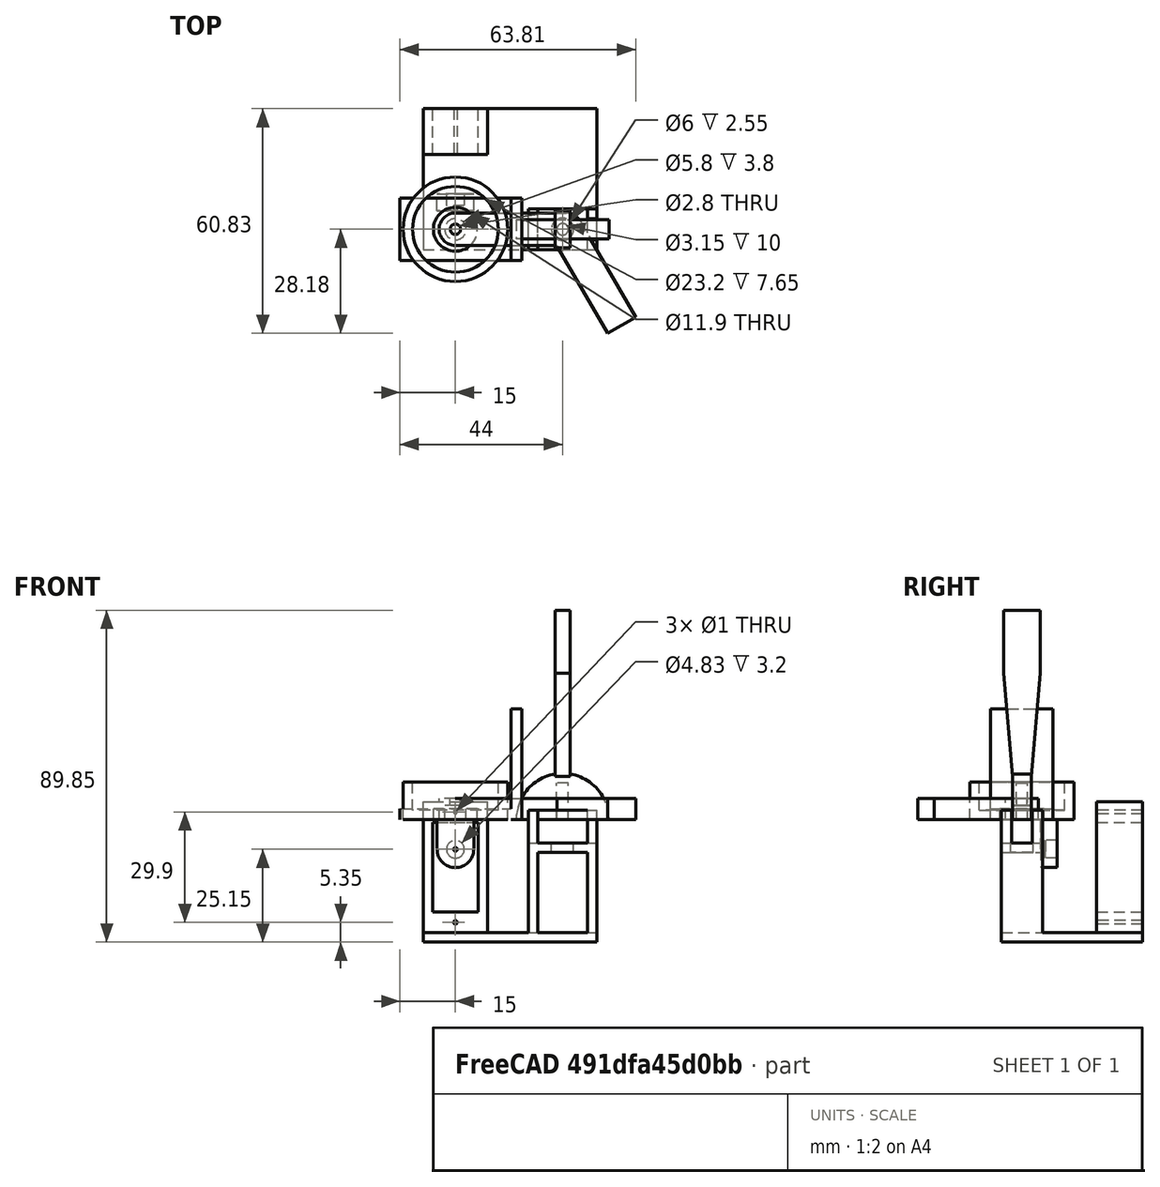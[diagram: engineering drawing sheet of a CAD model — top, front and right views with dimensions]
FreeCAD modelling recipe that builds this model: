
FCSTD DOCUMENT  (FreeCAD 0.18R16146 (Git))
Label: AnilloDedo
License: All rights reserved
LicenseURL: http://en.wikipedia.org/wiki/All_rights_reserved
objects: Part::Box×19, Part::Cylinder×15, Part::Cut×13, Part::MultiFuse×7, Spreadsheet::Sheet×1
note: 54 computed .brp shape members not serialized (recipe doc carries the construction recipe); baked Part::Feature solids carry a one-line shape summary decoded from their .brp

FEATURE [Spreadsheet::Sheet] Spreadsheet  label="v"
  cells = A1=Grosor; B1(Grosor)==2.55mm; A2=DiametroDedo; B2(DiametroDedo)==23.2mm; A3=AnilloMotorDiametro; B3(AnilloMotorDiametro)==4.83mm; A4=SeparacionDedoMotorGiro; B4(SeparacionDedoMotorGiro)==8mm; A5=AnilloMotorAlto; B5(AnilloMotorAlto)==3.2mm; A6=SeparacionDedoMotorHorizontal; B6(SeparacionDedoMotorHorizontal)==4.6mm; A7=PalancaSwitchDiametro; B7(PalancaSwitchDiametro)==3.15mm; A8=PalancaSwitchLargo; B8(PalancaSwitchLargo)==10mm; A9=SwitchDiametroRosca; B9(SwitchDiametroRosca)==6mm; A10=PalancaLargo; B10(PalancaLargo)==55mm; A11=PalancaAncho; B11(PalancaAncho)==10mm; A12=ServoAlto; B12(ServoAlto)==12.4mm; A13=ServoLargo; B13(ServoLargo)==22.4mm; A14=ServoAncho; B14(ServoAncho)==24.3mm; A15=ServoSeparacionTornillos; B15(ServoSeparacionTornillos)==26.8mm; A16=ServoAltoOreja; B16(ServoAltoOreja)==5.6mm; A17=ServoDistanciaEjeMotor; B17(ServoDistanciaEjeMotor)==17mm; A18=ServoDistanciaEjeOreja; B18(ServoDistanciaEjeOreja)==8.300000000000001mm; A19=ServoGrosorOreja; B19(ServoGrosorOreja)==2.4mm; A20=DistanciaDedoSwitch; B20(DistanciaDedoSwitch)==29mm; A21=SwitchLongRosca; B21(SwitchLongRosca)==8.800000000000001mm; A22=SwitchLargo; B22(SwitchLargo)==13.5mm
FEATURE [Part::Cylinder] Cylinder  label="PalancaHueco"
  Angle = 360
  AttacherType = Attacher::AttachEngine3D
  Height = 10
  Radius = 1.575
  expr: Height = v.PalancaSwitchLargo
  expr: Radius = v.PalancaSwitchDiametro / 2
FEATURE [Part::Cylinder] Cylinder001  label="PalancaCarril"
  Angle = 180
  AttacherType = Attacher::AttachEngine3D
  Height = 5.1
  Placement = pos=(0,2.55,0) rot=(1,0,0;1.5708rad)
  Radius = 12.55
  expr: Placement.Base.y = PalancaCarril.Height / 2
  expr: Radius = PalancaHueco.Height + v.Grosor
  expr: Height = v.Grosor * 2
FEATURE [Part::Box] Box  label="PalancaPala"
  AttacherType = Attacher::AttachEngine3D
  Height = 45
  Length = 4.125
  Placement = pos=(-2.0625,-5,11.7) rot=(0,0,1;0rad)
  Width = 10
  expr: Placement.Base.z = PalancaCarril.Radius - v.Grosor / 3
  expr: Placement.Base.y = -PalancaPala.Width / 2
  expr: Length = v.Grosor + v.PalancaSwitchDiametro / 2
  expr: Width = v.PalancaAncho
  expr: Placement.Base.x = -PalancaPala.Length / 2
  expr: Height = v.PalancaLargo - v.PalancaSwitchLargo
FEATURE [Part::Box] Box001  label="PalancaPalaQuita"
  AttacherType = Attacher::AttachEngine3D
  Height = 45
  Length = 4.125
  Placement = pos=(-2.0625,2.55,11.7) rot=(-1,0,0;0.087266rad)
  Width = 10
  expr: Placement.Base.z = PalancaPala.Placement.Base.z
  expr: Placement.Base.y = PalancaCarril.Height / 2
  expr: Placement.Base.x = PalancaPala.Placement.Base.x
  expr: Height = PalancaPala.Height
  expr: Width = PalancaPala.Width
  expr: Length = PalancaPala.Length
FEATURE [Part::Box] Box002  label="PalancaPalaQuita001"
  AttacherType = Attacher::AttachEngine3D
  Height = 45
  Length = 4.125
  Placement = pos=(2.0625,-2.55,11.7) rot=(0,-0.043619,0.999048;3.14159rad)
  Width = 10
  expr: Placement.Base.z = PalancaPala.Placement.Base.z
  expr: Placement.Base.y = -PalancaCarril.Height / 2
  expr: Placement.Base.x = PalancaPalaQuita001.Length / 2
  expr: Height = PalancaPala.Height
  expr: Width = PalancaPala.Width
  expr: Length = PalancaPala.Length
FEATURE [Part::Cut] Cut
  Base = -> Box
  Tool = -> Box001
FEATURE [Part::Cut] Cut001
  Base = -> Cut
  Tool = -> Box002
FEATURE [Part::MultiFuse] Fusion
  Shapes = -> [Cut001,Cylinder001]
FEATURE [Part::Cut] Cut002  label="Palanca"
  Base = -> Fusion
  Placement = pos=(29,0,0) rot=(0,0,1;0rad)
  Refine = true
  Tool = -> Cylinder
  expr: Placement.Base.x = TaladroSwitch.Placement.Base.x
FEATURE [Part::Cylinder] Cylinder002  label="AnilloInterior"
  Angle = 360
  AttacherType = Attacher::AttachEngine3D
  Height = 7.65
  Placement = pos=(0,0,2.55) rot=(0,0,1;0rad)
  Radius = 11.6
  expr: Placement.Base.z = v.Grosor
  expr: Height = v.Grosor * 3
  expr: Radius = v.DiametroDedo / 2
FEATURE [Part::Cylinder] Cylinder003  label="AnilloExterior"
  Angle = 360
  AttacherType = Attacher::AttachEngine3D
  Height = 10.2
  Radius = 14.15
  expr: Height = AnilloInterior.Height + v.Grosor
  expr: Radius = AnilloInterior.Radius + v.Grosor
FEATURE [Part::Cylinder] Cylinder004  label="MotorInterior"
  Angle = 360
  AttacherType = Attacher::AttachEngine3D
  Height = 3.2
  Placement = pos=(0,9.55,-8) rot=(1,0,0;1.5708rad)
  Radius = 2.415
  expr: Placement.Base.z = -v.SeparacionDedoMotorGiro
  expr: Placement.Base.y = AnilloExterior.Radius - v.SeparacionDedoMotorHorizontal
  expr: Height = v.AnilloMotorAlto
  expr: Radius = v.AnilloMotorDiametro / 2
FEATURE [Part::Cylinder] Cylinder005  label="MotorExterior"
  Angle = 360
  AttacherType = Attacher::AttachEngine3D
  Height = 4.475
  Placement = pos=(0,9.55,-8) rot=(1,0,0;1.5708rad)
  Radius = 4.965
  expr: Placement.Base.z = MotorInterior.Placement.Base.z
  expr: Placement.Base.y = MotorInterior.Placement.Base.y
  expr: Placement.Base.x = MotorInterior.Placement.Base.x
  expr: Height = MotorInterior.Height + v.Grosor / 2
  expr: Radius = MotorInterior.Radius + v.Grosor
FEATURE [Part::Cylinder] Cylinder006  label="TaladroTornilloAnilloMotor"
  Angle = 360
  AttacherType = Attacher::AttachEngine3D
  Height = 8.95
  Placement = pos=(0,9.55,-8) rot=(1,0,0;1.5708rad)
  Radius = 0.5
  expr: Placement.Base.z = MotorInterior.Placement.Base.z
  expr: Placement.Base.y = MotorInterior.Placement.Base.y
  expr: Placement.Base.x = MotorInterior.Placement.Base.x
  expr: Height = MotorExterior.Height * 2
  expr: Radius = 0.5mm
FEATURE [Part::Box] Box003  label="Radio"
  AttacherType = Attacher::AttachEngine3D
  Height = 8
  Length = 9.93
  Placement = pos=(-4.965,5.075,-8) rot=(0,0,1;0rad)
  Width = 4.475
  expr: Length = MotorExterior.Radius * 2
  expr: Width = MotorExterior.Height
  expr: Placement.Base.z = MotorInterior.Placement.Base.z
  expr: Placement.Base.y = MotorInterior.Placement.Base.y - Radio.Width
  expr: Height = MotorExterior.Placement.Base.z * -1
  expr: Placement.Base.x = MotorInterior.Placement.Base.x - Radio.Length / 2
FEATURE [Part::MultiFuse] Fusion001
  Shapes = -> [Cylinder003,Box003,Cylinder005]
FEATURE [Part::Cut] Cut003
  Base = -> Fusion001
  Tool = -> Cylinder002
FEATURE [Part::Cut] Cut004
  Base = -> Cut003
  Tool = -> Cylinder004
FEATURE [Part::Cut] Cut005  label="SoporteDedo"
  Base = -> Cut004
  Tool = -> Cylinder006
FEATURE [Part::Box] Box004  label="BaseServo"
  AttacherType = Attacher::AttachEngine3D
  Height = 5.6
  Length = 12.4
  Placement = pos=(-6.2,20.25,-30.6) rot=(0,0,1;0rad)
  Width = 12.4
  expr: Placement.Base.y = MotorInterior.Placement.Base.y + v.ServoDistanciaEjeOreja + v.ServoGrosorOreja
  expr: Placement.Base.z = TaladroTornilloAnilloMotor.Placement.Base.z - BaseServo.Height - v.ServoDistanciaEjeMotor
  expr: Length = v.ServoAlto
  expr: Width = v.ServoAlto
  expr: Placement.Base.x = -BaseServo.Length / 2
  expr: Height = v.ServoAltoOreja
FEATURE [Part::Cylinder] Cylinder007  label="TaladroAnclajeServo"
  Angle = 360
  AttacherType = Attacher::AttachEngine3D
  Height = 12.4
  Placement = pos=(0,32.65,-27.8) rot=(1,0,0;1.5708rad)
  Radius = 0.5
  expr: Placement.Base.y = BaseServo.Placement.Base.y + BaseServo.Width
  expr: Placement.Base.z = BaseServo.Placement.Base.z + BaseServo.Height / 2
  expr: Height = BaseServo.Width
  expr: Radius = TaladroTornilloAnilloMotor.Radius
FEATURE [Part::Box] Box005  label="LadoCajaServo"
  AttacherType = Attacher::AttachEngine3D
  Height = 35.5
  Length = 2.55
  Placement = pos=(-8.75,20.25,-30.6) rot=(0,0,1;0rad)
  Width = 12.4
  expr: Placement.Base.z = BaseServo.Placement.Base.z
  expr: Placement.Base.y = BaseServo.Placement.Base.y
  expr: Placement.Base.x = BaseServo.Placement.Base.x - v.Grosor
  expr: Height = BaseServo.Height + v.ServoAncho + TopServo.Height
  expr: Length = v.Grosor
  expr: Width = BaseServo.Width
FEATURE [Part::Box] Box006  label="LadoCajaServo001"
  AttacherType = Attacher::AttachEngine3D
  Height = 35.5
  Length = 2.55
  Placement = pos=(6.2,20.25,-30.6) rot=(0,0,1;0rad)
  Width = 12.4
  expr: Placement.Base.z = BaseServo.Placement.Base.z
  expr: Placement.Base.y = BaseServo.Placement.Base.y
  expr: Placement.Base.x = BaseServo.Placement.Base.x - v.Grosor + BaseServo.Width + v.Grosor
  expr: Height = BaseServo.Height + v.ServoAncho + TopServo.Height
  expr: Length = v.Grosor
  expr: Width = BaseServo.Width
FEATURE [Part::Box] Box007  label="TopServo"
  AttacherType = Attacher::AttachEngine3D
  Height = 5.6
  Length = 12.4
  Placement = pos=(-6.2,20.25,-0.7) rot=(0,0,1;0rad)
  Width = 12.4
  expr: Placement.Base.z = BaseServo.Placement.Base.z + v.ServoAncho + TopServo.Height
  expr: Placement.Base.y = BaseServo.Placement.Base.y
  expr: Placement.Base.x = BaseServo.Placement.Base.x
  expr: Height = BaseServo.Height
  expr: Width = BaseServo.Width
  expr: Length = BaseServo.Length
FEATURE [Part::Cylinder] Cylinder008  label="TaladroAnclajeServo001"
  Angle = 360
  AttacherType = Attacher::AttachEngine3D
  Height = 12.4
  Placement = pos=(0,32.65,2.1) rot=(1,0,0;1.5708rad)
  Radius = 0.5
  expr: Placement.Base.y = TopServo.Placement.Base.y + TopServo.Width
  expr: Placement.Base.z = TopServo.Placement.Base.z + TopServo.Height / 2
  expr: Height = BaseServo.Width
  expr: Radius = TaladroTornilloAnilloMotor.Radius
FEATURE [Part::Cylinder] Cylinder009  label="TaladroSwitch"
  Angle = 360
  AttacherType = Attacher::AttachEngine3D
  Height = 7.65
  Placement = pos=(29,0,-8.8) rot=(0,0,1;0rad)
  Radius = 3
  expr: Placement.Base.z = -v.SwitchLongRosca
  expr: Placement.Base.x = v.DistanciaDedoSwitch
  expr: Height = v.Grosor * 3
  expr: Radius = v.SwitchDiametroRosca / 2
FEATURE [Part::Box] Box008  label="BaseSwitch"
  AttacherType = Attacher::AttachEngine3D
  Height = 2.55
  Length = 13.5
  Placement = pos=(22.25,-5.55,-8.8) rot=(0,0,1;0rad)
  Width = 11.1
  expr: Placement.Base.z = TaladroSwitch.Placement.Base.z
  expr: Placement.Base.y = TaladroSwitch.Placement.Base.y - BaseSwitch.Width / 2
  expr: Length = v.SwitchLargo
  expr: Width = v.SwitchDiametroRosca + v.Grosor * 2
  expr: Placement.Base.x = TaladroSwitch.Placement.Base.x - BaseSwitch.Length / 2
  expr: Height = v.Grosor
FEATURE [Part::Box] Box009  label="Suelo"
  AttacherType = Attacher::AttachEngine3D
  Height = 2.55
  Length = 47.05
  Placement = pos=(-8.75,32.65,-30.6) rot=(1,0,0;3.14159rad)
  Width = 38.2
  expr: Length = -Suelo.Placement.Base.x + BaseSwitch001.Placement.Base.x + BaseSwitch001.Length + v.Grosor
  expr: Width = Suelo.Placement.Base.y + BaseSwitch001.Width / 2
  expr: Placement.Base.z = LadoCajaServo.Placement.Base.z
  expr: Placement.Base.y = LadoCajaServo.Placement.Base.y + LadoCajaServo.Width
  expr: Placement.Base.x = LadoCajaServo.Placement.Base.x
  expr: Height = v.Grosor
FEATURE [Part::Box] Box010  label="LadoCajaSwitch"
  AttacherType = Attacher::AttachEngine3D
  Height = 33.15
  Length = 2.55
  Placement = pos=(19.7,-5.55,-30.6) rot=(0,0,1;0rad)
  Width = 11.1
  expr: Placement.Base.y = BaseSwitch001.Placement.Base.y
  expr: Placement.Base.z = Suelo.Placement.Base.z
  expr: Placement.Base.x = BaseSwitch001.Placement.Base.x - v.Grosor
  expr: Height = -Suelo.Placement.Base.z + v.Grosor
  expr: Length = v.Grosor
  expr: Width = BaseSwitch001.Width
FEATURE [Part::Box] Box011  label="LadoCajaSwitch001"
  AttacherType = Attacher::AttachEngine3D
  Height = 33.15
  Length = 2.55
  Placement = pos=(35.75,-5.55,-30.6) rot=(0,0,1;0rad)
  Width = 11.1
  expr: Placement.Base.y = BaseSwitch001.Placement.Base.y
  expr: Placement.Base.z = Suelo.Placement.Base.z
  expr: Placement.Base.x = BaseSwitch001.Placement.Base.x + BaseSwitch001.Length
  expr: Height = -Suelo.Placement.Base.z + v.Grosor
  expr: Length = v.Grosor
  expr: Width = BaseSwitch001.Width
FEATURE [Part::Box] Box012  label="BaseSwitch001"
  AttacherType = Attacher::AttachEngine3D
  Height = 2.55
  Length = 13.5
  Placement = pos=(22.25,-5.55,0) rot=(0,0,1;0rad)
  Width = 11.1
  expr: Width = BaseSwitch.Width
  expr: Length = BaseSwitch.Length
  expr: Placement.Base.z = BaseSwitch.Placement.Base.z + v.SwitchLongRosca
  expr: Placement.Base.y = BaseSwitch.Placement.Base.y
  expr: Placement.Base.x = BaseSwitch.Placement.Base.x
  expr: Height = v.Grosor
FEATURE [Part::Box] Box013  label="QuitaCarril"
  AttacherType = Attacher::AttachEngine3D
  Height = 11.35
  Length = 18.6
  Placement = pos=(19.7,-2.8,-6.25) rot=(0,0,1;0rad)
  Width = 5.6
  expr: Placement.Base.z = BaseSwitch.Placement.Base.z + v.Grosor
  expr: Placement.Base.y = BaseSwitch.Placement.Base.y + (BaseSwitch.Width - QuitaCarril.Width) / 2
  expr: Length = BaseSwitch.Length + v.Grosor * 2
  expr: Width = PalancaCarril.Height + 0.5mm
  expr: Placement.Base.x = BaseSwitch.Placement.Base.x - v.Grosor
  expr: Height = v.Grosor + v.SwitchLongRosca
FEATURE [Part::MultiFuse] Fusion002  label="BaseSinTaladar"
  Shapes = -> [Box011,Box010,Box008,Box009,Box007,Box006,Box005,Box004]
FEATURE [Part::Cut] Cut006
  Base = -> Fusion002
  Tool = -> Box013
FEATURE [Part::Cut] Cut007
  Base = -> Cut006
  Tool = -> Cylinder009
FEATURE [Part::Cut] Cut008
  Base = -> Cut007
  Tool = -> Cylinder008
FEATURE [Part::Cut] Cut009  label="SoporteConjunto"
  Base = -> Cut008
  Tool = -> Cylinder007
FEATURE [Part::Cylinder] Cylinder010  label="InteriorServoGrande"
  Angle = 360
  AttacherType = Attacher::AttachEngine3D
  Height = 3.8
  Radius = 2.9
  expr: Radius = (5.9 - 0.1) / 2
FEATURE [Part::Cylinder] Cylinder011  label="ExteriorServoGrande"
  Angle = 360
  AttacherType = Attacher::AttachEngine3D
  Height = 5.8
  Radius = 4.4
  expr: Height = InteriorServoGrande.Height + 2mm
  expr: Radius = InteriorServoGrande.Radius + 1.5mm
FEATURE [Part::Cylinder] Cylinder012  label="TaladroServoGrande"
  Angle = 360
  AttacherType = Attacher::AttachEngine3D
  Height = 5.8
  Radius = 1.4
  expr: Height = ExteriorServoGrande.Height
  expr: Radius = 2.8 / 2
FEATURE [Part::Box] Box014  label="BaseRadioServoGrande"
  AttacherType = Attacher::AttachEngine3D
  Height = 5.8
  Length = 30
  Placement = pos=(0,-4.4,0) rot=(0,0,1;0rad)
  Width = 8.8
  expr: Placement.Base.y = -BaseRadioServoGrande.Width / 2
  expr: Width = ExteriorServoGrande.Radius * 2
  expr: Placement.Base.x = 0
  expr: Height = ExteriorServoGrande.Height
FEATURE [Part::MultiFuse] Fusion003
  Shapes = -> [Box014,Cylinder011]
FEATURE [Part::Cut] Cut010
  Base = -> Fusion003
  Tool = -> Cylinder012
FEATURE [Part::Cut] Cut011  label="RadioServoGrande"
  Base = -> Cut010
  Tool = -> Cylinder010
FEATURE [Part::Cylinder] Cylinder013  label="TaladroSwitchGordo"
  Angle = 360
  AttacherType = Attacher::AttachEngine3D
  Height = 3
  Radius = 5.95
  expr: Radius = 11.9 / 2
FEATURE [Part::Box] Box015  label="FrenteSwitchGordo"
  AttacherType = Attacher::AttachEngine3D
  Height = 3
  Length = 30
  Placement = pos=(-15,-8.45,0) rot=(0,0,1;0rad)
  Width = 16.9
  expr: Placement.Base.y = -FrenteSwitchGordo.Width / 2
  expr: Placement.Base.x = -FrenteSwitchGordo.Length / 2
  expr: Length = 30mm
  expr: Width = TaladroSwitchGordo.Radius * 2 + 5mm
FEATURE [Part::Box] Box016  label="BaseFrenteSwitchGordo"
  AttacherType = Attacher::AttachEngine3D
  Height = 30
  Length = 3
  Placement = pos=(15,-8.45,0) rot=(0,0,1;0rad)
  Width = 16.9
  expr: Width = FrenteSwitchGordo.Width
  expr: Placement.Base.y = -FrenteSwitchGordo.Width / 2
  expr: Placement.Base.x = FrenteSwitchGordo.Length / 2
  expr: Height = FrenteSwitchGordo.Length
FEATURE [Part::MultiFuse] Fusion004
  Shapes = -> [Box015,Box016]
FEATURE [Part::Cut] Cut012  label="L_SwitchGordo"
  Base = -> Fusion004
  Tool = -> Cylinder013
FEATURE [Part::Cylinder] Cylinder014  label="Rotula"
  Angle = 360
  AttacherType = Attacher::AttachEngine3D
  Height = 5.8
  Placement = pos=(30,0,0) rot=(0,0,1;0rad)
  Radius = 4.4
  expr: Placement.Base.x = BaseRadioServoGrande.Length
  expr: Height = InteriorServoGrande.Height + 2mm
  expr: Radius = InteriorServoGrande.Radius + 1.5mm
FEATURE [Part::Box] Box017  label="MedioRadioFlotante"
  AttacherType = Attacher::AttachEngine3D
  Height = 5.8
  Length = 30
  Width = 4.4
  expr: Height = BaseRadioServoGrande.Height
  expr: Width = BaseRadioServoGrande.Width / 2
  expr: Length = BaseRadioServoGrande.Length
FEATURE [Part::Box] Box018  label="MedioRadioFlotante001"
  AttacherType = Attacher::AttachEngine3D
  Height = 5.8
  Length = 30
  Placement = pos=(0,0,5.8) rot=(1,0,0;3.14159rad)
  Width = 4.4
  expr: Placement.Base.z = MedioRadioFlotante001.Height
  expr: Height = BaseRadioServoGrande.Height
  expr: Width = BaseRadioServoGrande.Width / 2
  expr: Length = BaseRadioServoGrande.Length
FEATURE [Part::MultiFuse] Fusion005  label="RadioFlotante"
  Placement = pos=(30,0,0) rot=(0,0,1;-1.0472rad)
  Shapes = -> [Box017,Box018]
  expr: Placement.Base.z = Rotula.Placement.Base.z
  expr: Placement.Base.y = Rotula.Placement.Base.y
  expr: Placement.Base.x = Rotula.Placement.Base.x
FEATURE [Part::MultiFuse] Fusion006  label="RadioCurvo"
  Shapes = -> [Cut011,Cylinder014,Fusion005]
